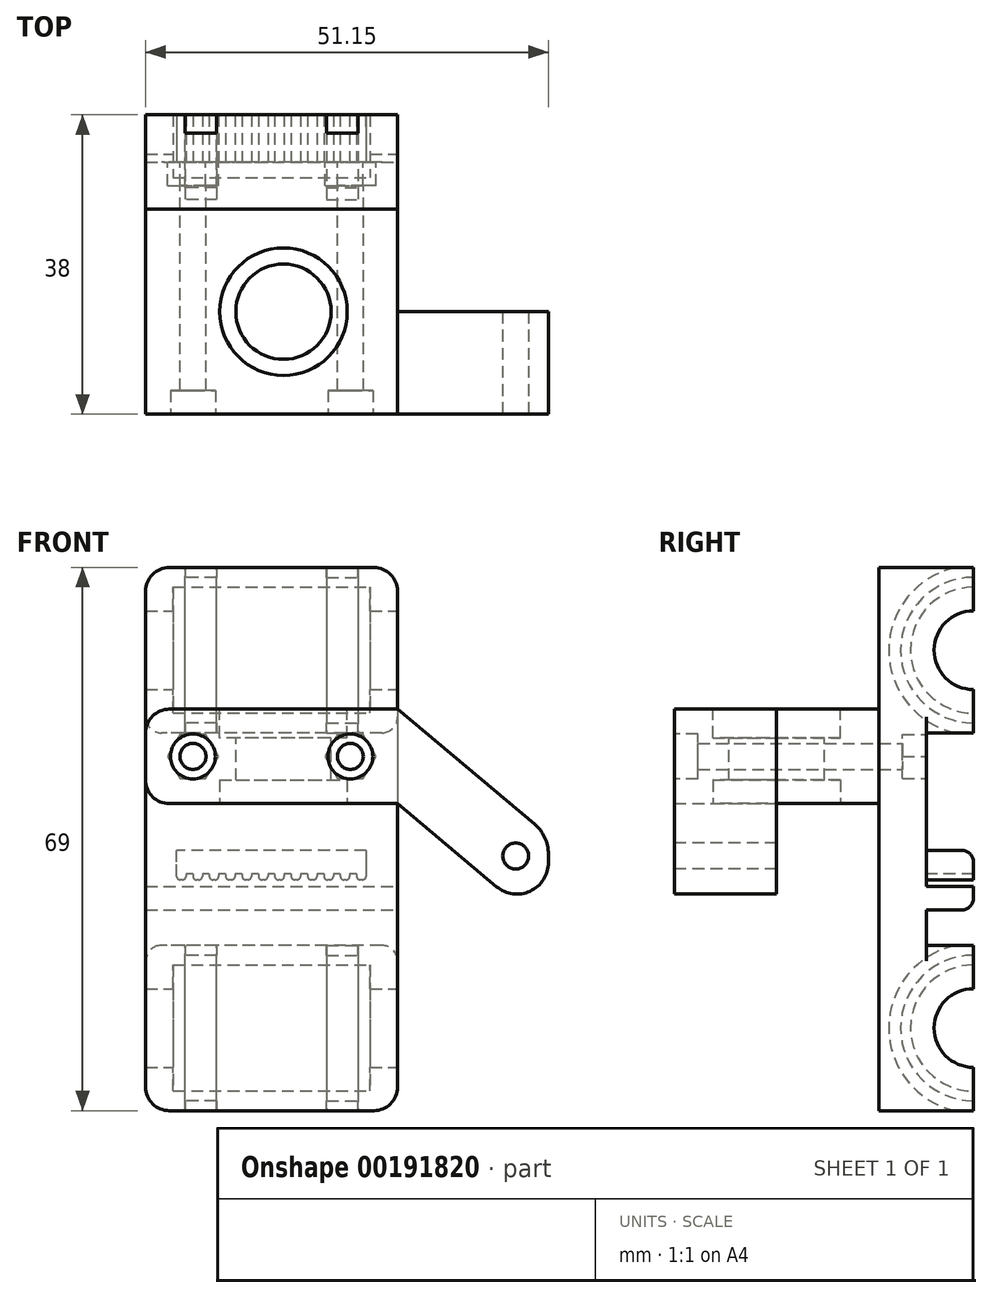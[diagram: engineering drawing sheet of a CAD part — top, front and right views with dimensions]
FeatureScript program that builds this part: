
annotation { "Feature Type Name" : "Feature", "Feature Type Description" : "" }
export const myFeature = defineFeature(function(context is Context, id is Id, definition is map)
    precondition{}
    {
        {
            var Q0;
            Q0=qCreatedBy(makeId("Front.planeOp"),FACE);
            var sketch = newSketch(context, id + "F0", { "sketchPlane" : qUnion([Q0])});
            skLineSegment(sketch, "E0.bottom", {"start": v(-16, 34.5) * mm, "end": v(16, 34.5) * mm});
            skLineSegment(sketch, "E0.top", {"start": v(-16, -34.5) * mm, "end": v(16, -34.5) * mm});
            skLineSegment(sketch, "E0.left", {"start": v(-16, 34.5) * mm, "end": v(-16, -34.5) * mm});
            skLineSegment(sketch, "E0.right", {"start": v(16, 34.5) * mm, "end": v(16, -34.5) * mm});
            skPoint(sketch, "E0.middle", {"position": v(0, 0) * mm});
            skLineSegment(sketch, "E1.bottom", {"start": v(-30, 24) * mm, "end": v(30, 24) * mm, "construction": true});
            skLineSegment(sketch, "E1.top", {"start": v(-30, -24) * mm, "end": v(30, -24) * mm, "construction": true});
            skLineSegment(sketch, "E1.left", {"start": v(-30, 24) * mm, "end": v(-30, -24) * mm, "construction": true});
            skLineSegment(sketch, "E1.right", {"start": v(30, 24) * mm, "end": v(30, -24) * mm, "construction": true});
            skSolve(sketch);
        }
        {
            var Q0;
            Q0=makeQuery(id+"F0.imprint","IMPRINT",FACE,{"disambiguationData":[TD([[makeQuery(id+"F0.imprint","IMPRINT",EDGE,{"derivedFrom":sQuery(id+"F0.wireOp",EDGE,"E0.bottom")}),-1.0]])]});
            extrude(context, id + "F1", {"entities" : qUnion([Q0]), "depth" : 6 * mm});
        }
        {
            var Q0;
            Q0=makeQuery(id+"F0.imprint","IMPRINT",FACE,{"disambiguationData":[TD([[makeQuery(id+"F0.imprint","IMPRINT",EDGE,{"derivedFrom":sQuery(id+"F0.wireOp",EDGE,"E0.bottom")}),-1.0]])]});
            var sketch = newSketch(context, id + "F2", { "sketchPlane" : qUnion([Q0])});
            skLineSegment(sketch, "E2.bottom", {"start": v(16, 34.5) * mm, "end": v(-16, 34.5) * mm});
            skLineSegment(sketch, "E2.top", {"start": v(16, 13.5) * mm, "end": v(-16, 13.5) * mm});
            skLineSegment(sketch, "E2.left", {"start": v(16, 34.5) * mm, "end": v(16, 13.5) * mm});
            skLineSegment(sketch, "E2.right", {"start": v(-16, 34.5) * mm, "end": v(-16, 13.5) * mm});
            skPoint(sketch, "E2.middle", {"position": v(0, 24) * mm});
            skLineSegment(sketch, "E3.bottom", {"start": v(16, -13.5) * mm, "end": v(-16, -13.5) * mm});
            skLineSegment(sketch, "E3.top", {"start": v(16, -34.5) * mm, "end": v(-16, -34.5) * mm});
            skLineSegment(sketch, "E3.left", {"start": v(16, -13.5) * mm, "end": v(16, -34.5) * mm});
            skLineSegment(sketch, "E3.right", {"start": v(-16, -13.5) * mm, "end": v(-16, -34.5) * mm});
            skPoint(sketch, "E3.middle", {"position": v(0, -24) * mm});
            skSolve(sketch);
        }
        {
            var Q0;
            Q0=makeQuery(id+"F2.imprint","IMPRINT",FACE,{"disambiguationData":[TD([[makeQuery(id+"F2.imprint","IMPRINT",EDGE,{"derivedFrom":sQuery(id+"F2.wireOp",EDGE,"E2.bottom")}),-1.0]])]});
            var Q1;
            Q1=makeQuery(id+"F2.imprint","IMPRINT",FACE,{"disambiguationData":[TD([[makeQuery(id+"F2.imprint","IMPRINT",EDGE,{"derivedFrom":sQuery(id+"F2.wireOp",EDGE,"E3.bottom")}),1.0]])]});
            extrude(context, id + "F3", {"entities" : qUnion([Q0, Q1]), "operationType" : NewBodyOperationType.ADD, "oppositeDirection" : true, "depth" : 6 * mm});
        }
        {
            var Q0;
            Q0=makeQuery(id+"F3.boolean.opBoolean","MERGE",FACE,{"derivedFrom":[makeQuery(id+"F1.opExtrude","SWEPT_FACE",FACE,{"disambiguationData":[OSD([sQuery(id+"F0.wireOp",EDGE,"E0.right")])]}),makeQuery(id+"F3.opExtrude","SWEPT_FACE",FACE,{"disambiguationData":[OSD([sQuery(id+"F2.wireOp",EDGE,"E2.left")])]}),makeQuery(id+"F3.opExtrude","SWEPT_FACE",FACE,{"disambiguationData":[OSD([sQuery(id+"F2.wireOp",EDGE,"E3.left")])]})]});
            cPlane(context, id + "F4", {"entities" : qUnion([Q0]), "cplaneType" : CPlaneType.OFFSET, "offset" : 3.5 * mm, "oppositeDirection" : true, "width" : 150 * mm, "height" : 150 * mm});
        }
        {
            var Q0;
            Q0=qCreatedBy(id+"F4.planeOp",FACE);
            var sketch = newSketch(context, id + "F5", { "sketchPlane" : qUnion([Q0])});
            skCircle(sketch, "E4", {"center": v(6, 24) * mm, "radius": 8 * mm});
            skCircle(sketch, "E5", {"center": v(6, -24) * mm, "radius": 8 * mm});
            skSolve(sketch);
        }
        {
            var Q0;
            Q0=makeQuery(id+"F5.imprint","IMPRINT",FACE,{"disambiguationData":[TD([[makeQuery(id+"F5.imprint","IMPRINT",EDGE,{"derivedFrom":sQuery(id+"F5.wireOp",EDGE,"E4")}),1.0]])]});
            var Q1;
            Q1=makeQuery(id+"F5.imprint","IMPRINT",FACE,{"disambiguationData":[TD([[makeQuery(id+"F5.imprint","IMPRINT",EDGE,{"derivedFrom":sQuery(id+"F5.wireOp",EDGE,"E5")}),1.0]])]});
            extrude(context, id + "F6", {"entities" : qUnion([Q0, Q1]), "operationType" : NewBodyOperationType.REMOVE, "oppositeDirection" : true, "depth" : 25 * mm});
        }
        {
            var Q0;
            Q0=makeQuery(id+"F3.boolean.opBoolean","MERGE",FACE,{"derivedFrom":[makeQuery(id+"F1.opExtrude","SWEPT_FACE",FACE,{"disambiguationData":[OSD([sQuery(id+"F0.wireOp",EDGE,"E0.right")])]}),makeQuery(id+"F3.opExtrude","SWEPT_FACE",FACE,{"disambiguationData":[OSD([sQuery(id+"F2.wireOp",EDGE,"E2.left")])]}),makeQuery(id+"F3.opExtrude","SWEPT_FACE",FACE,{"disambiguationData":[OSD([sQuery(id+"F2.wireOp",EDGE,"E3.left")])]})]});
            var sketch = newSketch(context, id + "F7", { "sketchPlane" : qUnion([Q0])});
            skCircle(sketch, "E6", {"center": v(6, 24) * mm, "radius": 5 * mm});
            skCircle(sketch, "E7", {"center": v(6, -24) * mm, "radius": 5 * mm});
            skSolve(sketch);
        }
        {
            var Q0;
            {var subQ0=sQuery(id+"F7.wireOp",EDGE,"E6");var subQ1=makeQuery(id+"F3.opExtrude","CAP_EDGE",EDGE,{"disambiguationData":[OSD([sQuery(id+"F2.wireOp",EDGE,"E2.left")])],"isStart":false});var subQ2=makeQuery(id+"F7.imprint","INTERSECT",VERTEX,{"disambiguationData":[OD(0.0)],"derivedFrom":[subQ1,subQ0]});Q0=makeQuery(id+"F7.imprint","IMPRINT",FACE,{"disambiguationData":[TD([[makeQuery(id+"F7.imprint","IMPRINT",EDGE,{"disambiguationData":[TD([[subQ2,-1.0]])],"derivedFrom":subQ0}),1.0]])]});}
            var Q1;
            {var subQ0=sQuery(id+"F7.wireOp",EDGE,"E7");var subQ1=makeQuery(id+"F3.opExtrude","CAP_EDGE",EDGE,{"disambiguationData":[OSD([sQuery(id+"F2.wireOp",EDGE,"E3.left")])],"isStart":false});var subQ2=makeQuery(id+"F7.imprint","INTERSECT",VERTEX,{"disambiguationData":[OD(0.0)],"derivedFrom":[subQ1,subQ0]});Q1=makeQuery(id+"F7.imprint","IMPRINT",FACE,{"disambiguationData":[TD([[makeQuery(id+"F7.imprint","IMPRINT",EDGE,{"disambiguationData":[TD([[subQ2,1.0]])],"derivedFrom":subQ0}),1.0]])]});}
            var Q2;
            Q2=makeQuery(id+"F3.boolean.opBoolean","MERGE",FACE,{"derivedFrom":[makeQuery(id+"F1.opExtrude","SWEPT_FACE",FACE,{"disambiguationData":[OSD([sQuery(id+"F0.wireOp",EDGE,"E0.left")])]}),makeQuery(id+"F3.opExtrude","SWEPT_FACE",FACE,{"disambiguationData":[OSD([sQuery(id+"F2.wireOp",EDGE,"E2.right")])]}),makeQuery(id+"F3.opExtrude","SWEPT_FACE",FACE,{"disambiguationData":[OSD([sQuery(id+"F2.wireOp",EDGE,"E3.right")])]})]});
            extrude(context, id + "F8", {"entities" : qUnion([Q0, Q1]), "operationType" : NewBodyOperationType.REMOVE, "endBound" : BoundingType.UP_TO_SURFACE, "oppositeDirection" : true, "endBoundEntityFace" : qUnion([Q2]), "depth" : 25 * mm});
        }
        {
            var Q0;
            Q0=makeQuery(id+"F3.boolean.opBoolean","MERGE",FACE,{"derivedFrom":[makeQuery(id+"F1.opExtrude","SWEPT_FACE",FACE,{"disambiguationData":[OSD([sQuery(id+"F0.wireOp",EDGE,"E0.right")])]}),makeQuery(id+"F3.opExtrude","SWEPT_FACE",FACE,{"disambiguationData":[OSD([sQuery(id+"F2.wireOp",EDGE,"E2.left")])]}),makeQuery(id+"F3.opExtrude","SWEPT_FACE",FACE,{"disambiguationData":[OSD([sQuery(id+"F2.wireOp",EDGE,"E3.left")])]})]});
            cPlane(context, id + "F9", {"entities" : qUnion([Q0]), "cplaneType" : CPlaneType.OFFSET, "offset" : 5 * mm, "oppositeDirection" : true, "width" : 150 * mm, "height" : 150 * mm});
        }
        {
            var Q0;
            Q0=makeQuery(id+"F3.boolean.opBoolean","MERGE",FACE,{"derivedFrom":[makeQuery(id+"F1.opExtrude","SWEPT_FACE",FACE,{"disambiguationData":[OSD([sQuery(id+"F0.wireOp",EDGE,"E0.left")])]}),makeQuery(id+"F3.opExtrude","SWEPT_FACE",FACE,{"disambiguationData":[OSD([sQuery(id+"F2.wireOp",EDGE,"E2.right")])]}),makeQuery(id+"F3.opExtrude","SWEPT_FACE",FACE,{"disambiguationData":[OSD([sQuery(id+"F2.wireOp",EDGE,"E3.right")])]})]});
            cPlane(context, id + "F10", {"entities" : qUnion([Q0]), "cplaneType" : CPlaneType.OFFSET, "offset" : 5 * mm, "oppositeDirection" : true, "width" : 150 * mm, "height" : 150 * mm});
        }
        {
            var Q0;
            Q0=qCreatedBy(id+"F9.planeOp",FACE);
            var sketch = newSketch(context, id + "F11", { "sketchPlane" : qUnion([Q0])});
            skCircle(sketch, "E8", {"center": v(6, 24) * mm, "radius": 9.25 * mm});
            skCircle(sketch, "E9", {"center": v(6, 24) * mm, "radius": 10.75 * mm});
            skCircle(sketch, "E10", {"center": v(6, -24) * mm, "radius": 10.75 * mm});
            skCircle(sketch, "E11", {"center": v(6, -24) * mm, "radius": 9.25 * mm});
            skSolve(sketch);
        }
        {
            var Q0;
            Q0=makeQuery(id+"F11.imprint","IMPRINT",FACE,{"disambiguationData":[TD([[makeQuery(id+"F11.imprint","IMPRINT",EDGE,{"derivedFrom":sQuery(id+"F11.wireOp",EDGE,"E8")}),-1.0]])]});
            var Q1;
            Q1=makeQuery(id+"F11.imprint","IMPRINT",FACE,{"disambiguationData":[TD([[makeQuery(id+"F11.imprint","IMPRINT",EDGE,{"derivedFrom":sQuery(id+"F11.wireOp",EDGE,"E10")}),1.0]])]});
            extrude(context, id + "F12", {"entities" : qUnion([Q0, Q1]), "operationType" : NewBodyOperationType.REMOVE, "oppositeDirection" : true, "depth" : 4 * mm});
        }
        {
            var Q0;
            Q0=qCreatedBy(id+"F10.planeOp",FACE);
            var sketch = newSketch(context, id + "F13", { "sketchPlane" : qUnion([Q0])});
            skCircle(sketch, "E12", {"center": v(-6, 24) * mm, "radius": 10.75 * mm});
            skCircle(sketch, "E13", {"center": v(-6, 24) * mm, "radius": 9.25 * mm});
            skCircle(sketch, "E14", {"center": v(-6, -24) * mm, "radius": 10.75 * mm});
            skCircle(sketch, "E15", {"center": v(-6, -24) * mm, "radius": 9.25 * mm});
            skSolve(sketch);
        }
        {
            var Q0;
            Q0=makeQuery(id+"F13.imprint","IMPRINT",FACE,{"disambiguationData":[TD([[makeQuery(id+"F13.imprint","IMPRINT",EDGE,{"derivedFrom":sQuery(id+"F13.wireOp",EDGE,"E12")}),1.0]])]});
            var Q1;
            Q1=makeQuery(id+"F13.imprint","IMPRINT",FACE,{"disambiguationData":[TD([[makeQuery(id+"F13.imprint","IMPRINT",EDGE,{"derivedFrom":sQuery(id+"F13.wireOp",EDGE,"E14")}),1.0]])]});
            extrude(context, id + "F14", {"entities" : qUnion([Q0, Q1]), "operationType" : NewBodyOperationType.REMOVE, "oppositeDirection" : true, "depth" : 4 * mm});
        }
        {
            var Q0;
            Q0=makeQuery(id+"F3.opExtrude","SWEPT_EDGE",EDGE,{"disambiguationData":[OSD([sQuery(id+"F0.wireOp",EDGE,"E0.right"),sQuery(id+"F2.wireOp",EDGE,"E2.top"),sQuery(id+"F2.wireOp",EDGE,"E2.left")])]});
            var Q1;
            Q1=makeQuery(id+"F3.opExtrude","SWEPT_EDGE",EDGE,{"disambiguationData":[OSD([sQuery(id+"F0.wireOp",EDGE,"E0.left"),sQuery(id+"F2.wireOp",EDGE,"E2.top"),sQuery(id+"F2.wireOp",EDGE,"E2.right")])]});
            var Q2;
            Q2=makeQuery(id+"F3.opExtrude","SWEPT_EDGE",EDGE,{"disambiguationData":[OSD([sQuery(id+"F0.wireOp",EDGE,"E0.right"),sQuery(id+"F2.wireOp",EDGE,"E3.bottom"),sQuery(id+"F2.wireOp",EDGE,"E3.left")])]});
            var Q3;
            Q3=makeQuery(id+"F3.opExtrude","SWEPT_EDGE",EDGE,{"disambiguationData":[OSD([sQuery(id+"F0.wireOp",EDGE,"E0.left"),sQuery(id+"F2.wireOp",EDGE,"E3.bottom"),sQuery(id+"F2.wireOp",EDGE,"E3.right")])]});
            fillet(context, id + "F15", {"entities" : qUnion([Q0, Q1, Q2, Q3]), "radius" : 2 * mm, "tangentPropagation" : true, "allowEdgeOverflow" : false});
        }
        {
            var Q0;
            Q0=makeQuery(id+"F3.boolean.opBoolean","MERGE",EDGE,{"derivedFrom":[makeQuery(id+"F1.opExtrude","SWEPT_EDGE",EDGE,{"disambiguationData":[OSD([sQuery(id+"F0.wireOp",EDGE,"E0.top"),sQuery(id+"F0.wireOp",EDGE,"E0.right")])]}),makeQuery(id+"F3.opExtrude","SWEPT_EDGE",EDGE,{"disambiguationData":[OSD([sQuery(id+"F2.wireOp",EDGE,"E3.top"),sQuery(id+"F2.wireOp",EDGE,"E3.left")])]})]});
            var Q1;
            Q1=makeQuery(id+"F3.boolean.opBoolean","MERGE",EDGE,{"derivedFrom":[makeQuery(id+"F1.opExtrude","SWEPT_EDGE",EDGE,{"disambiguationData":[OSD([sQuery(id+"F0.wireOp",EDGE,"E0.top"),sQuery(id+"F0.wireOp",EDGE,"E0.left")])]}),makeQuery(id+"F3.opExtrude","SWEPT_EDGE",EDGE,{"disambiguationData":[OSD([sQuery(id+"F2.wireOp",EDGE,"E3.top"),sQuery(id+"F2.wireOp",EDGE,"E3.right")])]})]});
            var Q2;
            Q2=makeQuery(id+"F3.boolean.opBoolean","MERGE",EDGE,{"derivedFrom":[makeQuery(id+"F1.opExtrude","SWEPT_EDGE",EDGE,{"disambiguationData":[OSD([sQuery(id+"F0.wireOp",EDGE,"E0.bottom"),sQuery(id+"F0.wireOp",EDGE,"E0.right")])]}),makeQuery(id+"F3.opExtrude","SWEPT_EDGE",EDGE,{"disambiguationData":[OSD([sQuery(id+"F2.wireOp",EDGE,"E2.bottom"),sQuery(id+"F2.wireOp",EDGE,"E2.left")])]})]});
            var Q3;
            Q3=makeQuery(id+"F3.boolean.opBoolean","MERGE",EDGE,{"derivedFrom":[makeQuery(id+"F1.opExtrude","SWEPT_EDGE",EDGE,{"disambiguationData":[OSD([sQuery(id+"F0.wireOp",EDGE,"E0.bottom"),sQuery(id+"F0.wireOp",EDGE,"E0.left")])]}),makeQuery(id+"F3.opExtrude","SWEPT_EDGE",EDGE,{"disambiguationData":[OSD([sQuery(id+"F2.wireOp",EDGE,"E2.bottom"),sQuery(id+"F2.wireOp",EDGE,"E2.right")])]})]});
            fillet(context, id + "F16", {"entities" : qUnion([Q0, Q1, Q2, Q3]), "radius" : 3 * mm, "tangentPropagation" : true, "allowEdgeOverflow" : false});
        }
        {
            var Q0;
            Q0=makeQuery(id+"F1.opExtrude","CAP_FACE",FACE,{"disambiguationData":[OSD([sQuery(id+"F0.wireOp",EDGE,"E0.bottom"),sQuery(id+"F0.wireOp",EDGE,"E0.top"),sQuery(id+"F0.wireOp",EDGE,"E0.left"),sQuery(id+"F0.wireOp",EDGE,"E0.right")])],"isStart":true});
            var sketch = newSketch(context, id + "F17", { "sketchPlane" : qUnion([Q0])});
            skCircle(sketch, "E16", {"center": v(-10, 10.5) * mm, "radius": 1.65 * mm});
            skCircle(sketch, "E17", {"center": v(10, 10.5) * mm, "radius": 1.65 * mm});
            skCircle(sketch, "E18.cCircle", {"center": v(-10, 10.5) * mm, "radius": 2.8 * mm, "construction": true});
            skLineSegment(sketch, "E18.0", {"start": v(-13.23, 10.5) * mm, "end": v(-11.62, 13.3) * mm});
            skLineSegment(sketch, "E18.1", {"start": v(-11.62, 13.3) * mm, "end": v(-8.38, 13.3) * mm});
            skLineSegment(sketch, "E18.2", {"start": v(-8.38, 13.3) * mm, "end": v(-6.77, 10.5) * mm});
            skLineSegment(sketch, "E18.3", {"start": v(-6.77, 10.5) * mm, "end": v(-8.38, 7.7) * mm});
            skLineSegment(sketch, "E18.4", {"start": v(-8.38, 7.7) * mm, "end": v(-11.62, 7.7) * mm});
            skLineSegment(sketch, "E18.5", {"start": v(-11.62, 7.7) * mm, "end": v(-13.23, 10.5) * mm});
            skPoint(sketch, "E18.0.midPoint", {"position": v(-12.42, 11.9) * mm});
            skCircle(sketch, "E19.cCircle", {"center": v(10, 10.5) * mm, "radius": 2.8 * mm, "construction": true});
            skLineSegment(sketch, "E19.0", {"start": v(6.77, 10.5) * mm, "end": v(8.38, 13.3) * mm});
            skLineSegment(sketch, "E19.1", {"start": v(8.38, 13.3) * mm, "end": v(11.62, 13.3) * mm});
            skLineSegment(sketch, "E19.2", {"start": v(11.62, 13.3) * mm, "end": v(13.23, 10.5) * mm});
            skLineSegment(sketch, "E19.3", {"start": v(13.23, 10.5) * mm, "end": v(11.62, 7.7) * mm});
            skLineSegment(sketch, "E19.4", {"start": v(11.62, 7.7) * mm, "end": v(8.38, 7.7) * mm});
            skLineSegment(sketch, "E19.5", {"start": v(8.38, 7.7) * mm, "end": v(6.77, 10.5) * mm});
            skPoint(sketch, "E19.0.midPoint", {"position": v(7.58, 11.9) * mm});
            skSolve(sketch);
        }
        {
            var Q0;
            Q0=makeQuery(id+"F17.imprint","IMPRINT",FACE,{"disambiguationData":[TD([[makeQuery(id+"F17.imprint","IMPRINT",EDGE,{"derivedFrom":sQuery(id+"F17.wireOp",EDGE,"E16")}),1.0]])]});
            var Q1;
            Q1=makeQuery(id+"F17.imprint","IMPRINT",FACE,{"disambiguationData":[TD([[makeQuery(id+"F17.imprint","IMPRINT",EDGE,{"derivedFrom":sQuery(id+"F17.wireOp",EDGE,"E17")}),1.0]])]});
            extrude(context, id + "F18", {"entities" : qUnion([Q0, Q1]), "operationType" : NewBodyOperationType.REMOVE, "endBound" : BoundingType.THROUGH_ALL, "oppositeDirection" : true, "depth" : 25 * mm});
        }
        {
            var Q0;
            Q0=makeQuery(id+"F17.imprint","IMPRINT",FACE,{"disambiguationData":[TD([[makeQuery(id+"F17.imprint","IMPRINT",EDGE,{"derivedFrom":sQuery(id+"F17.wireOp",EDGE,"E16")}),-1.0]])]});
            var Q1;
            Q1=makeQuery(id+"F17.imprint","IMPRINT",FACE,{"disambiguationData":[TD([[makeQuery(id+"F17.imprint","IMPRINT",EDGE,{"derivedFrom":sQuery(id+"F17.wireOp",EDGE,"E17")}),-1.0]])]});
            extrude(context, id + "F19", {"entities" : qUnion([Q0, Q1]), "operationType" : NewBodyOperationType.REMOVE, "oppositeDirection" : true, "depth" : 3 * mm});
        }
        {
            var Q0;
            Q0=makeQuery(id+"F1.opExtrude","CAP_FACE",FACE,{"disambiguationData":[OSD([sQuery(id+"F0.wireOp",EDGE,"E0.bottom"),sQuery(id+"F0.wireOp",EDGE,"E0.top"),sQuery(id+"F0.wireOp",EDGE,"E0.left"),sQuery(id+"F0.wireOp",EDGE,"E0.right")])],"isStart":false});
            var sketch = newSketch(context, id + "F20", { "sketchPlane" : qUnion([Q0])});
            skLineSegment(sketch, "E20.bottom", {"start": v(-16, 16.5) * mm, "end": v(16, 16.5) * mm});
            skLineSegment(sketch, "E20.top", {"start": v(-16, 4.5) * mm, "end": v(16, 4.5) * mm});
            skLineSegment(sketch, "E20.left", {"start": v(-16, 16.5) * mm, "end": v(-16, 4.5) * mm});
            skLineSegment(sketch, "E20.right", {"start": v(16, 16.5) * mm, "end": v(16, 4.5) * mm});
            skSolve(sketch);
        }
        {
            var Q0;
            Q0=makeQuery(id+"F20.imprint","IMPRINT",FACE,{"disambiguationData":[TD([[makeQuery(id+"F20.imprint","IMPRINT",EDGE,{"derivedFrom":sQuery(id+"F20.wireOp",EDGE,"E20.bottom")}),-1.0]])]});
            extrude(context, id + "F21", {"entities" : qUnion([Q0]), "depth" : (26 / 2) * mm});
        }
        {
            var Q0;
            Q0=makeQuery(id+"F21.opExtrude","CAP_FACE",FACE,{"disambiguationData":[OSD([sQuery(id+"F0.wireOp",EDGE,"E0.bottom"),sQuery(id+"F0.wireOp",EDGE,"E0.top"),sQuery(id+"F0.wireOp",EDGE,"E0.left"),sQuery(id+"F0.wireOp",EDGE,"E0.right"),sQuery(id+"F17.wireOp",EDGE,"E16"),sQuery(id+"F17.wireOp",EDGE,"E17"),sQuery(id+"F20.wireOp",EDGE,"E20.bottom"),sQuery(id+"F20.wireOp",EDGE,"E20.top"),sQuery(id+"F20.wireOp",EDGE,"E20.left"),sQuery(id+"F20.wireOp",EDGE,"E20.right")])],"isStart":false});
            extrude(context, id + "F22", {"entities" : qUnion([Q0]), "depth" : (26 / 2) * mm});
        }
        {
            var Q0;
            Q0=makeQuery(id+"F21.opExtrude","SWEPT_EDGE",EDGE,{"disambiguationData":[OSD([sQuery(id+"F0.wireOp",EDGE,"E0.left"),sQuery(id+"F20.wireOp",EDGE,"E20.top"),sQuery(id+"F20.wireOp",EDGE,"E20.left")])]});
            var Q1;
            Q1=makeQuery(id+"F22.opExtrude","SWEPT_EDGE",EDGE,{"disambiguationData":[OSD([sQuery(id+"F0.wireOp",EDGE,"E0.left"),sQuery(id+"F20.wireOp",EDGE,"E20.top"),sQuery(id+"F20.wireOp",EDGE,"E20.left")])]});
            var Q2;
            Q2=makeQuery(id+"F22.opExtrude","SWEPT_EDGE",EDGE,{"disambiguationData":[OSD([sQuery(id+"F0.wireOp",EDGE,"E0.left"),sQuery(id+"F20.wireOp",EDGE,"E20.bottom"),sQuery(id+"F20.wireOp",EDGE,"E20.left")])]});
            var Q3;
            Q3=makeQuery(id+"F21.opExtrude","SWEPT_EDGE",EDGE,{"disambiguationData":[OSD([sQuery(id+"F0.wireOp",EDGE,"E0.left"),sQuery(id+"F20.wireOp",EDGE,"E20.bottom"),sQuery(id+"F20.wireOp",EDGE,"E20.left")])]});
            fillet(context, id + "F23", {"entities" : qUnion([Q0, Q1, Q2, Q3]), "radius" : 3 * mm, "tangentPropagation" : true, "allowEdgeOverflow" : false});
        }
        {
            var Q0;
            Q0=makeQuery(id+"F21.opExtrude","SWEPT_FACE",FACE,{"disambiguationData":[OSD([sQuery(id+"F20.wireOp",EDGE,"E20.bottom")])]});
            var sketch = newSketch(context, id + "F24", { "sketchPlane" : qUnion([Q0])});
            skCircle(sketch, "E21", {"center": v(1.5, -19) * mm, "radius": 8.1 * mm});
            skSolve(sketch);
        }
        {
            var Q0;
            {var subQ0=sQuery(id+"F24.wireOp",EDGE,"E21");var subQ1=makeQuery(id+"F21.opExtrude","CAP_EDGE",EDGE,{"disambiguationData":[OSD([sQuery(id+"F20.wireOp",EDGE,"E20.bottom")])],"isStart":false});var subQ2=makeQuery(id+"F24.imprint","INTERSECT",VERTEX,{"disambiguationData":[OD(0.0)],"derivedFrom":[subQ1,subQ0]});Q0=makeQuery(id+"F24.imprint","IMPRINT",FACE,{"disambiguationData":[TD([[makeQuery(id+"F24.imprint","IMPRINT",EDGE,{"disambiguationData":[TD([[subQ2,1.0]])],"derivedFrom":subQ0}),1.0]])]});}
            var Q1;
            {var subQ0=sQuery(id+"F24.wireOp",EDGE,"E21");var subQ1=makeQuery(id+"F21.opExtrude","CAP_EDGE",EDGE,{"disambiguationData":[OSD([sQuery(id+"F20.wireOp",EDGE,"E20.bottom")])],"isStart":false});var subQ2=makeQuery(id+"F24.imprint","INTERSECT",VERTEX,{"disambiguationData":[OD(0.0)],"derivedFrom":[subQ1,subQ0]});Q1=makeQuery(id+"F24.imprint","IMPRINT",FACE,{"disambiguationData":[TD([[makeQuery(id+"F24.imprint","IMPRINT",EDGE,{"disambiguationData":[TD([[subQ2,-1.0]])],"derivedFrom":subQ0}),1.0]])]});}
            extrude(context, id + "F25", {"entities" : qUnion([Q0, Q1]), "operationType" : NewBodyOperationType.REMOVE, "oppositeDirection" : true, "depth" : 3.65 * mm});
        }
        {
            var Q0;
            Q0=makeQuery(id+"F21.opExtrude","SWEPT_FACE",FACE,{"disambiguationData":[OSD([sQuery(id+"F20.wireOp",EDGE,"E20.top")])]});
            var sketch = newSketch(context, id + "F26", { "sketchPlane" : qUnion([Q0])});
            skCircle(sketch, "E22", {"center": v(1.5, 19) * mm, "radius": 8.1 * mm});
            skSolve(sketch);
        }
        {
            var Q0;
            {var subQ0=sQuery(id+"F26.wireOp",EDGE,"E22");var subQ1=makeQuery(id+"F21.opExtrude","CAP_EDGE",EDGE,{"disambiguationData":[OSD([sQuery(id+"F20.wireOp",EDGE,"E20.top")])],"isStart":false});var subQ2=makeQuery(id+"F26.imprint","INTERSECT",VERTEX,{"disambiguationData":[OD(0.0)],"derivedFrom":[subQ1,subQ0]});Q0=makeQuery(id+"F26.imprint","IMPRINT",FACE,{"disambiguationData":[TD([[makeQuery(id+"F26.imprint","IMPRINT",EDGE,{"disambiguationData":[TD([[subQ2,1.0]])],"derivedFrom":subQ0}),1.0]])]});}
            var Q1;
            {var subQ0=sQuery(id+"F26.wireOp",EDGE,"E22");var subQ1=makeQuery(id+"F21.opExtrude","CAP_EDGE",EDGE,{"disambiguationData":[OSD([sQuery(id+"F20.wireOp",EDGE,"E20.top")])],"isStart":false});var subQ2=makeQuery(id+"F26.imprint","INTERSECT",VERTEX,{"disambiguationData":[OD(0.0)],"derivedFrom":[subQ1,subQ0]});Q1=makeQuery(id+"F26.imprint","IMPRINT",FACE,{"disambiguationData":[TD([[makeQuery(id+"F26.imprint","IMPRINT",EDGE,{"disambiguationData":[TD([[subQ2,-1.0]])],"derivedFrom":subQ0}),1.0]])]});}
            extrude(context, id + "F27", {"entities" : qUnion([Q0, Q1]), "operationType" : NewBodyOperationType.REMOVE, "oppositeDirection" : true, "depth" : 3 * mm});
        }
        {
            var Q0;
            {var subQ0=sQuery(id+"F24.wireOp",EDGE,"E21");Q0=makeQuery(id+"F25.boolean.opBoolean","COPY",FACE,{"disambiguationData":[TD([makeQuery(id+"F21.opExtrude","CAP_FACE",FACE,{"disambiguationData":[OSD([sQuery(id+"F0.wireOp",EDGE,"E0.bottom"),sQuery(id+"F0.wireOp",EDGE,"E0.top"),sQuery(id+"F0.wireOp",EDGE,"E0.left"),sQuery(id+"F0.wireOp",EDGE,"E0.right"),sQuery(id+"F17.wireOp",EDGE,"E16"),sQuery(id+"F17.wireOp",EDGE,"E17"),sQuery(id+"F20.wireOp",EDGE,"E20.bottom"),sQuery(id+"F20.wireOp",EDGE,"E20.top"),sQuery(id+"F20.wireOp",EDGE,"E20.left"),sQuery(id+"F20.wireOp",EDGE,"E20.right")])],"isStart":false})])],"derivedFrom":makeQuery(id+"F25.opExtrude","CAP_FACE",FACE,{"disambiguationData":[OSD([subQ0])],"isStart":false})});}
            var sketch = newSketch(context, id + "F28", { "sketchPlane" : qUnion([Q0])});
            skCircle(sketch, "E23", {"center": v(1.5, -19) * mm, "radius": 6.05 * mm});
            skSolve(sketch);
        }
        {
            var Q0;
            {var subQ0=sQuery(id+"F28.wireOp",EDGE,"E23");var subQ1=makeQuery(id+"F25.boolean.opBoolean","INTERSECT",EDGE,{"derivedFrom":[makeQuery(id+"F21.opExtrude","CAP_FACE",FACE,{"disambiguationData":[OSD([sQuery(id+"F0.wireOp",EDGE,"E0.bottom"),sQuery(id+"F0.wireOp",EDGE,"E0.top"),sQuery(id+"F0.wireOp",EDGE,"E0.left"),sQuery(id+"F0.wireOp",EDGE,"E0.right"),sQuery(id+"F17.wireOp",EDGE,"E16"),sQuery(id+"F17.wireOp",EDGE,"E17"),sQuery(id+"F20.wireOp",EDGE,"E20.bottom"),sQuery(id+"F20.wireOp",EDGE,"E20.top"),sQuery(id+"F20.wireOp",EDGE,"E20.left"),sQuery(id+"F20.wireOp",EDGE,"E20.right")])],"isStart":false}),makeQuery(id+"F25.opExtrude","CAP_FACE",FACE,{"disambiguationData":[OSD([sQuery(id+"F24.wireOp",EDGE,"E21")])],"isStart":false})]});var subQ2=makeQuery(id+"F28.imprint","INTERSECT",VERTEX,{"disambiguationData":[OD(0.0)],"derivedFrom":[subQ1,subQ0]});Q0=makeQuery(id+"F28.imprint","IMPRINT",FACE,{"disambiguationData":[TD([[makeQuery(id+"F28.imprint","IMPRINT",EDGE,{"disambiguationData":[TD([[subQ2,1.0]])],"derivedFrom":subQ0}),1.0]])]});}
            var Q1;
            {var subQ0=sQuery(id+"F28.wireOp",EDGE,"E23");var subQ1=makeQuery(id+"F25.boolean.opBoolean","INTERSECT",EDGE,{"derivedFrom":[makeQuery(id+"F21.opExtrude","CAP_FACE",FACE,{"disambiguationData":[OSD([sQuery(id+"F0.wireOp",EDGE,"E0.bottom"),sQuery(id+"F0.wireOp",EDGE,"E0.top"),sQuery(id+"F0.wireOp",EDGE,"E0.left"),sQuery(id+"F0.wireOp",EDGE,"E0.right"),sQuery(id+"F17.wireOp",EDGE,"E16"),sQuery(id+"F17.wireOp",EDGE,"E17"),sQuery(id+"F20.wireOp",EDGE,"E20.bottom"),sQuery(id+"F20.wireOp",EDGE,"E20.top"),sQuery(id+"F20.wireOp",EDGE,"E20.left"),sQuery(id+"F20.wireOp",EDGE,"E20.right")])],"isStart":false}),makeQuery(id+"F25.opExtrude","CAP_FACE",FACE,{"disambiguationData":[OSD([sQuery(id+"F24.wireOp",EDGE,"E21")])],"isStart":false})]});var subQ2=makeQuery(id+"F28.imprint","INTERSECT",VERTEX,{"disambiguationData":[OD(0.0)],"derivedFrom":[subQ1,subQ0]});Q1=makeQuery(id+"F28.imprint","IMPRINT",FACE,{"disambiguationData":[TD([[makeQuery(id+"F28.imprint","IMPRINT",EDGE,{"disambiguationData":[TD([[subQ2,-1.0]])],"derivedFrom":subQ0}),1.0]])]});}
            extrude(context, id + "F29", {"entities" : qUnion([Q0, Q1]), "operationType" : NewBodyOperationType.REMOVE, "oppositeDirection" : true, "depth" : 25 * mm});
        }
        {
            var Q0;
            Q0=makeQuery(id+"F22.opExtrude","CAP_FACE",FACE,{"disambiguationData":[OSD([sQuery(id+"F0.wireOp",EDGE,"E0.bottom"),sQuery(id+"F0.wireOp",EDGE,"E0.top"),sQuery(id+"F0.wireOp",EDGE,"E0.left"),sQuery(id+"F0.wireOp",EDGE,"E0.right"),sQuery(id+"F17.wireOp",EDGE,"E16"),sQuery(id+"F17.wireOp",EDGE,"E17"),sQuery(id+"F20.wireOp",EDGE,"E20.bottom"),sQuery(id+"F20.wireOp",EDGE,"E20.top"),sQuery(id+"F20.wireOp",EDGE,"E20.left"),sQuery(id+"F20.wireOp",EDGE,"E20.right")])],"isStart":false});
            var sketch = newSketch(context, id + "F30", { "sketchPlane" : qUnion([Q0])});
            skCircle(sketch, "E24", {"center": v(-10, 10.5) * mm, "radius": 2.85 * mm});
            skCircle(sketch, "E25", {"center": v(10, 10.5) * mm, "radius": 2.85 * mm});
            skSolve(sketch);
        }
        {
            var Q0;
            Q0=qSketchRegion(id+"F30",true);
            extrude(context, id + "F31", {"entities" : qUnion([Q0]), "operationType" : NewBodyOperationType.REMOVE, "oppositeDirection" : true, "depth" : 3 * mm});
        }
        {
            var Q0;
            Q0=makeQuery(id+"F0.imprint","IMPRINT",FACE,{"disambiguationData":[TD([[makeQuery(id+"F0.imprint","IMPRINT",EDGE,{"derivedFrom":sQuery(id+"F0.wireOp",EDGE,"E0.bottom")}),-1.0]])]});
            var sketch = newSketch(context, id + "F32", { "sketchPlane" : qUnion([Q0])});
            skLineSegment(sketch, "E26.bottom", {"start": v(-16, -9) * mm, "end": v(16, -9) * mm});
            skLineSegment(sketch, "E26.top", {"start": v(-16, -6) * mm, "end": v(16, -6) * mm});
            skLineSegment(sketch, "E26.left", {"start": v(-16, -9) * mm, "end": v(-16, -6) * mm});
            skLineSegment(sketch, "E26.right", {"start": v(16, -9) * mm, "end": v(16, -6) * mm});
            skLineSegment(sketch, "E27.bottom", {"start": v(12, -1.42) * mm, "end": v(-12, -1.42) * mm});
            skLineSegment(sketch, "E27.top", {"start": v(12, -4.42) * mm, "end": v(-12, -4.42) * mm});
            skLineSegment(sketch, "E27.left", {"start": v(12, -1.42) * mm, "end": v(12, -4.42) * mm});
            skLineSegment(sketch, "E27.right", {"start": v(-12, -1.42) * mm, "end": v(-12, -4.42) * mm});
            skLineSegment(sketch, "E28", {"start": v(7.4, -5.17) * mm, "end": v(7.1, -5.17) * mm});
            skLineSegment(sketch, "E29.bottom", {"start": v(12, -4.42) * mm, "end": v(10.8, -4.42) * mm, "construction": true});
            skLineSegment(sketch, "E29.top", {"start": v(11.55, -5.17) * mm, "end": v(11.25, -5.17) * mm});
            skLineSegment(sketch, "E29.left", {"start": v(12, -4.42) * mm, "end": v(12, -4.72) * mm});
            skLineSegment(sketch, "E29.right", {"start": v(10.8, -4.42) * mm, "end": v(10.8, -4.72) * mm});
            skLineSegment(sketch, "E30.bottom", {"start": v(9.92, -4.42) * mm, "end": v(8.72, -4.42) * mm, "construction": true});
            skLineSegment(sketch, "E30.top", {"start": v(9.92, -5.17) * mm, "end": v(8.72, -5.17) * mm});
            skLineSegment(sketch, "E30.left", {"start": v(9.92, -4.42) * mm, "end": v(9.92, -4.72) * mm});
            skLineSegment(sketch, "E30.right", {"start": v(8.72, -4.42) * mm, "end": v(8.72, -4.72) * mm});
            skLineSegment(sketch, "E31.1.0.0", {"start": v(7.84, -4.42) * mm, "end": v(7.84, -4.72) * mm});
            skLineSegment(sketch, "E31.1.0.1", {"start": v(6.64, -4.42) * mm, "end": v(6.64, -4.72) * mm});
            skLineSegment(sketch, "E31.2.0.0", {"start": v(5.76, -4.42) * mm, "end": v(5.76, -4.72) * mm});
            skLineSegment(sketch, "E31.2.0.1", {"start": v(4.56, -4.42) * mm, "end": v(4.56, -4.72) * mm});
            skLineSegment(sketch, "E31.3.0.0", {"start": v(3.68, -4.42) * mm, "end": v(3.68, -4.72) * mm});
            skLineSegment(sketch, "E31.3.0.1", {"start": v(2.48, -4.42) * mm, "end": v(2.48, -4.72) * mm});
            skLineSegment(sketch, "E31.4.0.0", {"start": v(1.6, -4.42) * mm, "end": v(1.6, -4.72) * mm});
            skLineSegment(sketch, "E31.4.0.1", {"start": v(0.4, -4.42) * mm, "end": v(0.4, -4.72) * mm});
            skLineSegment(sketch, "E31.5.0.0", {"start": v(-0.48, -4.42) * mm, "end": v(-0.48, -4.72) * mm});
            skLineSegment(sketch, "E31.5.0.1", {"start": v(-1.68, -4.42) * mm, "end": v(-1.68, -4.72) * mm});
            skLineSegment(sketch, "E31.6.0.0", {"start": v(-2.56, -4.42) * mm, "end": v(-2.56, -4.72) * mm});
            skLineSegment(sketch, "E31.6.0.1", {"start": v(-3.76, -4.42) * mm, "end": v(-3.76, -4.72) * mm});
            skLineSegment(sketch, "E31.7.0.0", {"start": v(-4.64, -4.42) * mm, "end": v(-4.64, -4.72) * mm});
            skLineSegment(sketch, "E31.7.0.1", {"start": v(-5.84, -4.42) * mm, "end": v(-5.84, -4.72) * mm});
            skLineSegment(sketch, "E31.8.0.0", {"start": v(-6.72, -4.42) * mm, "end": v(-6.72, -4.72) * mm});
            skLineSegment(sketch, "E31.8.0.1", {"start": v(-7.92, -4.42) * mm, "end": v(-7.92, -4.72) * mm});
            skLineSegment(sketch, "E31.9.0.0", {"start": v(-8.8, -4.42) * mm, "end": v(-8.8, -4.72) * mm});
            skLineSegment(sketch, "E31.9.0.1", {"start": v(-10, -4.42) * mm, "end": v(-10, -4.72) * mm});
            skLineSegment(sketch, "E31.direction1", {"start": v(9.47, -5.17) * mm, "end": v(9.17, -5.17) * mm, "construction": true});
            skPoint(sketch, "E32.visualSharp", {"position": v(12, -5.17) * mm});
            skArc(sketch, "E32.filletArc", {"start": v(11.55, -5.17) * mm, "mid": v(11.87, -5.04) * mm, "end": v(12, -4.72) * mm});
            skPoint(sketch, "E33.visualSharp", {"position": v(10.8, -5.17) * mm});
            skArc(sketch, "E33.filletArc", {"start": v(10.8, -4.72) * mm, "mid": v(10.93, -5.04) * mm, "end": v(11.25, -5.17) * mm});
            skPoint(sketch, "E34.visualSharp", {"position": v(9.92, -5.17) * mm});
            skArc(sketch, "E34.filletArc", {"start": v(9.47, -5.17) * mm, "mid": v(9.79, -5.04) * mm, "end": v(9.92, -4.72) * mm});
            skPoint(sketch, "E35.newPointA", {"position": v(7.84, -5.17) * mm});
            skPoint(sketch, "E35.newPointB", {"position": v(8.72, -5.17) * mm});
            skArc(sketch, "E35.filletArc", {"start": v(8.72, -4.72) * mm, "mid": v(8.85, -5.04) * mm, "end": v(9.17, -5.17) * mm});
            skPoint(sketch, "E36.newPointB", {"position": v(16, -5.17) * mm});
            skArc(sketch, "E36.filletArc", {"start": v(7.4, -5.17) * mm, "mid": v(7.7, -5.04) * mm, "end": v(7.84, -4.72) * mm});
            skPoint(sketch, "E37.newPointA", {"position": v(-16, -5.17) * mm});
            skPoint(sketch, "E37.newPointB", {"position": v(6.64, -5.17) * mm});
            skArc(sketch, "E37.filletArc", {"start": v(6.64, -4.72) * mm, "mid": v(6.77, -5.04) * mm, "end": v(7.1, -5.17) * mm});
            skLineSegment(sketch, "E38", {"start": v(5.31, -5.17) * mm, "end": v(5.01, -5.17) * mm});
            skLineSegment(sketch, "E39", {"start": v(3.23, -5.17) * mm, "end": v(2.93, -5.17) * mm});
            skLineSegment(sketch, "E40", {"start": v(1.15, -5.17) * mm, "end": v(0.85, -5.17) * mm});
            skLineSegment(sketch, "E41", {"start": v(-0.93, -5.17) * mm, "end": v(-1.23, -5.17) * mm});
            skLineSegment(sketch, "E42", {"start": v(-3, -5.17) * mm, "end": v(-3.3, -5.17) * mm});
            skLineSegment(sketch, "E43", {"start": v(-5.09, -5.17) * mm, "end": v(-5.39, -5.17) * mm});
            skLineSegment(sketch, "E44", {"start": v(-7.17, -5.17) * mm, "end": v(-7.47, -5.17) * mm});
            skLineSegment(sketch, "E45", {"start": v(-9.25, -5.17) * mm, "end": v(-9.55, -5.17) * mm});
            skPoint(sketch, "E46.visualSharp", {"position": v(5.76, -5.17) * mm});
            skArc(sketch, "E46.filletArc", {"start": v(5.31, -5.17) * mm, "mid": v(5.63, -5.04) * mm, "end": v(5.76, -4.72) * mm});
            skPoint(sketch, "E47.visualSharp", {"position": v(4.56, -5.17) * mm});
            skArc(sketch, "E47.filletArc", {"start": v(4.56, -4.72) * mm, "mid": v(4.7, -5.04) * mm, "end": v(5.01, -5.17) * mm});
            skPoint(sketch, "E48.visualSharp", {"position": v(3.68, -5.17) * mm});
            skArc(sketch, "E48.filletArc", {"start": v(3.23, -5.17) * mm, "mid": v(3.55, -5.04) * mm, "end": v(3.68, -4.72) * mm});
            skPoint(sketch, "E49.visualSharp", {"position": v(2.48, -5.17) * mm});
            skArc(sketch, "E49.filletArc", {"start": v(2.48, -4.72) * mm, "mid": v(2.61, -5.04) * mm, "end": v(2.93, -5.17) * mm});
            skPoint(sketch, "E50.visualSharp", {"position": v(1.6, -5.17) * mm});
            skArc(sketch, "E50.filletArc", {"start": v(1.15, -5.17) * mm, "mid": v(1.47, -5.04) * mm, "end": v(1.6, -4.72) * mm});
            skPoint(sketch, "E51.visualSharp", {"position": v(0.4, -5.17) * mm});
            skArc(sketch, "E51.filletArc", {"start": v(0.4, -4.72) * mm, "mid": v(0.53, -5.04) * mm, "end": v(0.85, -5.17) * mm});
            skPoint(sketch, "E52.visualSharp", {"position": v(-0.48, -5.17) * mm});
            skArc(sketch, "E52.filletArc", {"start": v(-0.93, -5.17) * mm, "mid": v(-0.61, -5.04) * mm, "end": v(-0.48, -4.72) * mm});
            skPoint(sketch, "E53.visualSharp", {"position": v(-1.68, -5.17) * mm});
            skArc(sketch, "E53.filletArc", {"start": v(-1.68, -4.72) * mm, "mid": v(-1.55, -5.04) * mm, "end": v(-1.23, -5.17) * mm});
            skPoint(sketch, "E54.visualSharp", {"position": v(-2.56, -5.17) * mm});
            skArc(sketch, "E54.filletArc", {"start": v(-3, -5.17) * mm, "mid": v(-2.7, -5.04) * mm, "end": v(-2.56, -4.72) * mm});
            skPoint(sketch, "E55.visualSharp", {"position": v(-3.76, -5.17) * mm});
            skArc(sketch, "E55.filletArc", {"start": v(-3.76, -4.72) * mm, "mid": v(-3.63, -5.04) * mm, "end": v(-3.3, -5.17) * mm});
            skPoint(sketch, "E56.visualSharp", {"position": v(-4.64, -5.17) * mm});
            skArc(sketch, "E56.filletArc", {"start": v(-5.09, -5.17) * mm, "mid": v(-4.77, -5.04) * mm, "end": v(-4.64, -4.72) * mm});
            skPoint(sketch, "E57.visualSharp", {"position": v(-5.84, -5.17) * mm});
            skArc(sketch, "E57.filletArc", {"start": v(-5.84, -4.72) * mm, "mid": v(-5.7, -5.04) * mm, "end": v(-5.39, -5.17) * mm});
            skPoint(sketch, "E58.visualSharp", {"position": v(-6.72, -5.17) * mm});
            skArc(sketch, "E58.filletArc", {"start": v(-7.17, -5.17) * mm, "mid": v(-6.85, -5.04) * mm, "end": v(-6.72, -4.72) * mm});
            skPoint(sketch, "E59.visualSharp", {"position": v(-8.8, -5.17) * mm});
            skArc(sketch, "E59.filletArc", {"start": v(-9.25, -5.17) * mm, "mid": v(-8.93, -5.04) * mm, "end": v(-8.8, -4.72) * mm});
            skPoint(sketch, "E60.visualSharp", {"position": v(-7.92, -5.17) * mm});
            skArc(sketch, "E60.filletArc", {"start": v(-7.92, -4.72) * mm, "mid": v(-7.79, -5.04) * mm, "end": v(-7.47, -5.17) * mm});
            skPoint(sketch, "E61.visualSharp", {"position": v(-10, -5.17) * mm});
            skArc(sketch, "E61.filletArc", {"start": v(-10, -4.72) * mm, "mid": v(-9.87, -5.04) * mm, "end": v(-9.55, -5.17) * mm});
            skLineSegment(sketch, "E62.bottom", {"start": v(-10.88, -4.42) * mm, "end": v(-12.08, -4.42) * mm});
            skLineSegment(sketch, "E62.top", {"start": v(-11.33, -5.17) * mm, "end": v(-11.63, -5.17) * mm});
            skLineSegment(sketch, "E62.left", {"start": v(-10.88, -4.42) * mm, "end": v(-10.88, -4.72) * mm});
            skLineSegment(sketch, "E62.right", {"start": v(-12.08, -4.42) * mm, "end": v(-12.08, -4.72) * mm});
            skPoint(sketch, "E63.visualSharp", {"position": v(-10.88, -5.17) * mm});
            skArc(sketch, "E63.filletArc", {"start": v(-11.33, -5.17) * mm, "mid": v(-11.01, -5.04) * mm, "end": v(-10.88, -4.72) * mm});
            skPoint(sketch, "E64.visualSharp", {"position": v(-12.08, -5.17) * mm});
            skArc(sketch, "E64.filletArc", {"start": v(-12.08, -4.72) * mm, "mid": v(-11.95, -5.04) * mm, "end": v(-11.63, -5.17) * mm});
            skLineSegment(sketch, "E65.bottom", {"start": v(-12.08, -4.42) * mm, "end": v(-12, -4.42) * mm});
            skLineSegment(sketch, "E65.top", {"start": v(-12.08, -1.42) * mm, "end": v(-12, -1.42) * mm});
            skLineSegment(sketch, "E65.left", {"start": v(-12.08, -4.42) * mm, "end": v(-12.08, -1.42) * mm});
            skLineSegment(sketch, "E65.right", {"start": v(-12, -4.42) * mm, "end": v(-12, -1.42) * mm});
            skLineSegment(sketch, "E66.bottom", {"start": v(1.68, -9) * mm, "end": v(-1.68, -9) * mm});
            skLineSegment(sketch, "E66.top", {"start": v(1.68, -6) * mm, "end": v(-1.68, -6) * mm});
            skLineSegment(sketch, "E66.left", {"start": v(1.68, -9) * mm, "end": v(1.68, -6) * mm});
            skLineSegment(sketch, "E66.right", {"start": v(-1.68, -9) * mm, "end": v(-1.68, -6) * mm});
            skSolve(sketch);
        }
        {
            var Q0;
            Q0=makeQuery(id+"F32.imprint","IMPRINT",FACE,{"disambiguationData":[TD([[makeQuery(id+"F32.imprint","IMPRINT",EDGE,{"derivedFrom":sQuery(id+"F32.wireOp",EDGE,"E27.bottom")}),1.0]])]});
            var Q1;
            Q1=makeQuery(id+"F32.imprint","IMPRINT",FACE,{"disambiguationData":[TD([[makeQuery(id+"F32.imprint","IMPRINT",EDGE,{"derivedFrom":sQuery(id+"F32.wireOp",EDGE,"E26.bottom")}),1.0]])]});
            var Q2;
            Q2=makeQuery(id+"F32.imprint","IMPRINT",FACE,{"disambiguationData":[TD([[makeQuery(id+"F32.imprint","IMPRINT",EDGE,{"derivedFrom":sQuery(id+"F32.wireOp",EDGE,"E29.top")}),-1.0]])]});
            var Q3;
            Q3=makeQuery(id+"F32.imprint","IMPRINT",FACE,{"disambiguationData":[TD([[makeQuery(id+"F32.imprint","IMPRINT",EDGE,{"derivedFrom":sQuery(id+"F32.wireOp",EDGE,"E28")}),-1.0]])]});
            var Q4;
            {var subQ1=sQuery(id+"F32.wireOp",EDGE,"E30.left");Q4=makeQuery(id+"F32.imprint","IMPRINT",FACE,{"disambiguationData":[TD([[makeQuery(id+"F32.imprint","IMPRINT",EDGE,{"derivedFrom":subQ1}),-1.0]])]});}
            var Q5;
            {var subQ1=sQuery(id+"F32.wireOp",EDGE,"E31.2.0.0");Q5=makeQuery(id+"F32.imprint","IMPRINT",FACE,{"disambiguationData":[TD([[makeQuery(id+"F32.imprint","IMPRINT",EDGE,{"derivedFrom":subQ1}),-1.0]])]});}
            var Q6;
            {var subQ1=sQuery(id+"F32.wireOp",EDGE,"E31.3.0.0");Q6=makeQuery(id+"F32.imprint","IMPRINT",FACE,{"disambiguationData":[TD([[makeQuery(id+"F32.imprint","IMPRINT",EDGE,{"derivedFrom":subQ1}),-1.0]])]});}
            var Q7;
            {var subQ1=sQuery(id+"F32.wireOp",EDGE,"E31.4.0.0");Q7=makeQuery(id+"F32.imprint","IMPRINT",FACE,{"disambiguationData":[TD([[makeQuery(id+"F32.imprint","IMPRINT",EDGE,{"derivedFrom":subQ1}),-1.0]])]});}
            var Q8;
            {var subQ0=sQuery(id+"F32.wireOp",EDGE,"E31.5.0.0");Q8=makeQuery(id+"F32.imprint","IMPRINT",FACE,{"disambiguationData":[TD([[makeQuery(id+"F32.imprint","IMPRINT",EDGE,{"derivedFrom":subQ0}),-1.0]])]});}
            var Q9;
            {var subQ1=sQuery(id+"F32.wireOp",EDGE,"E31.6.0.0");Q9=makeQuery(id+"F32.imprint","IMPRINT",FACE,{"disambiguationData":[TD([[makeQuery(id+"F32.imprint","IMPRINT",EDGE,{"derivedFrom":subQ1}),-1.0]])]});}
            var Q10;
            {var subQ0=sQuery(id+"F32.wireOp",EDGE,"E31.7.0.0");Q10=makeQuery(id+"F32.imprint","IMPRINT",FACE,{"disambiguationData":[TD([[makeQuery(id+"F32.imprint","IMPRINT",EDGE,{"derivedFrom":subQ0}),-1.0]])]});}
            var Q11;
            Q11=makeQuery(id+"F32.imprint","IMPRINT",FACE,{"disambiguationData":[TD([[makeQuery(id+"F32.imprint","IMPRINT",EDGE,{"derivedFrom":sQuery(id+"F32.wireOp",EDGE,"E65.bottom")}),1.0]])]});
            var Q12;
            {var subQ1=sQuery(id+"F32.wireOp",EDGE,"E31.8.0.0");Q12=makeQuery(id+"F32.imprint","IMPRINT",FACE,{"disambiguationData":[TD([[makeQuery(id+"F32.imprint","IMPRINT",EDGE,{"derivedFrom":subQ1}),-1.0]])]});}
            var Q13;
            {var subQ0=sQuery(id+"F32.wireOp",EDGE,"E31.9.0.0");Q13=makeQuery(id+"F32.imprint","IMPRINT",FACE,{"disambiguationData":[TD([[makeQuery(id+"F32.imprint","IMPRINT",EDGE,{"derivedFrom":subQ0}),-1.0]])]});}
            var Q14;
            Q14=makeQuery(id+"F32.imprint","IMPRINT",FACE,{"disambiguationData":[TD([[makeQuery(id+"F32.imprint","IMPRINT",EDGE,{"derivedFrom":sQuery(id+"F32.wireOp",EDGE,"E65.top")}),-1.0]])]});
            var Q15;
            Q15=makeQuery(id+"F32.imprint","IMPRINT",FACE,{"disambiguationData":[TD([[makeQuery(id+"F32.imprint","IMPRINT",EDGE,{"derivedFrom":sQuery(id+"F32.wireOp",EDGE,"E62.top")}),-1.0]])]});
            extrude(context, id + "F33", {"entities" : qUnion([Q0, Q1, Q2, Q3, Q4, Q5, Q6, Q7, Q8, Q9, Q10, Q11, Q12, Q13, Q14, Q15]), "operationType" : NewBodyOperationType.ADD, "oppositeDirection" : true, "depth" : 6 * mm});
        }
        {
            var Q0;
            Q0=makeQuery(id+"F33.opExtrude","CAP_EDGE",EDGE,{"disambiguationData":[OSD([sQuery(id+"F32.wireOp",EDGE,"E26.bottom")])],"isStart":false});
            var Q1;
            Q1=makeQuery(id+"F33.opExtrude","CAP_EDGE",EDGE,{"disambiguationData":[OSD([sQuery(id+"F32.wireOp",EDGE,"E27.bottom"),sQuery(id+"F32.wireOp",EDGE,"E65.top")])],"isStart":false});
            fillet(context, id + "F34", {"entities" : qUnion([Q0, Q1]), "radius" : 1.5 * mm, "tangentPropagation" : true, "allowEdgeOverflow" : false});
        }
        {
            var Q0;
            {var subQ0=sQuery(id+"F20.wireOp",EDGE,"E20.right");var subQ1=sQuery(id+"F20.wireOp",EDGE,"E20.top");var subQ2=sQuery(id+"F20.wireOp",EDGE,"E20.bottom");var subQ3=sQuery(id+"F17.wireOp",EDGE,"E16");var subQ4=sQuery(id+"F0.wireOp",EDGE,"E0.right");var subQ5=sQuery(id+"F0.wireOp",EDGE,"E0.left");var subQ6=sQuery(id+"F0.wireOp",EDGE,"E0.top");var subQ7=sQuery(id+"F0.wireOp",EDGE,"E0.bottom");var subQ8=makeQuery(id+"F21.opExtrude","CAP_FACE",FACE,{"disambiguationData":[OSD([subQ7,subQ6,subQ5,subQ4,subQ3,sQuery(id+"F17.wireOp",EDGE,"E17"),subQ2,subQ1,sQuery(id+"F20.wireOp",EDGE,"E20.left"),subQ0])],"isStart":false});Q0=makeQuery(id+"F29.boolean.opBoolean","SPLIT",FACE,{"disambiguationData":[TD([makeQuery(id+"F21.opExtrude","SWEPT_FACE",FACE,{"disambiguationData":[OSD([subQ0])]})])],"derivedFrom":subQ8});}
            var sketch = newSketch(context, id + "F35", { "sketchPlane" : qUnion([Q0])});
            skLineSegment(sketch, "E67", {"start": v(16, 16.5) * mm, "end": v(35.15, 0.43) * mm});
            skLineSegment(sketch, "E68", {"start": v(16, 4.5) * mm, "end": v(35.15, -11.57) * mm});
            skLineSegment(sketch, "E69", {"start": v(35.15, 0.43) * mm, "end": v(35.15, -11.57) * mm});
            skLineSegment(sketch, "E70", {"start": v(16, 16.5) * mm, "end": v(16, 4.5) * mm});
            skSolve(sketch);
        }
        {
            var Q0;
            {var subQ8=sQuery(id+"F35.wireOp",EDGE,"E67");Q0=makeQuery(id+"F35.imprint","IMPRINT",FACE,{"disambiguationData":[TD([[makeQuery(id+"F35.imprint","IMPRINT",EDGE,{"derivedFrom":subQ8}),-1.0]])]});}
            extrude(context, id + "F36", {"entities" : qUnion([Q0]), "operationType" : NewBodyOperationType.ADD, "depth" : 13 * mm});
        }
        {
            var Q0;
            Q0=makeQuery(id+"F36.opExtrude","SWEPT_EDGE",EDGE,{"disambiguationData":[OSD([sQuery(id+"F35.wireOp",EDGE,"E67"),sQuery(id+"F35.wireOp",EDGE,"E69")])]});
            fillet(context, id + "F37", {"entities" : qUnion([Q0]), "radius" : 5 * mm, "tangentPropagation" : true, "allowEdgeOverflow" : false});
        }
        {
            var Q0;
            Q0=makeQuery(id+"F36.opExtrude","SWEPT_EDGE",EDGE,{"disambiguationData":[OSD([sQuery(id+"F35.wireOp",EDGE,"E68"),sQuery(id+"F35.wireOp",EDGE,"E69")])]});
            fillet(context, id + "F38", {"entities" : qUnion([Q0]), "radius" : 4 * mm, "tangentPropagation" : true, "allowEdgeOverflow" : false});
        }
        {
            var Q0;
            Q0=makeQuery(id+"F36.boolean.opBoolean","MERGE",FACE,{"derivedFrom":[makeQuery(id+"F22.opExtrude","CAP_FACE",FACE,{"disambiguationData":[OSD([sQuery(id+"F0.wireOp",EDGE,"E0.bottom"),sQuery(id+"F0.wireOp",EDGE,"E0.top"),sQuery(id+"F0.wireOp",EDGE,"E0.left"),sQuery(id+"F0.wireOp",EDGE,"E0.right"),sQuery(id+"F17.wireOp",EDGE,"E16"),sQuery(id+"F17.wireOp",EDGE,"E17"),sQuery(id+"F20.wireOp",EDGE,"E20.bottom"),sQuery(id+"F20.wireOp",EDGE,"E20.top"),sQuery(id+"F20.wireOp",EDGE,"E20.left"),sQuery(id+"F20.wireOp",EDGE,"E20.right")])],"isStart":false}),makeQuery(id+"F36.opExtrude","CAP_FACE",FACE,{"disambiguationData":[OSD([sQuery(id+"F35.wireOp",EDGE,"E67"),sQuery(id+"F35.wireOp",EDGE,"E68"),sQuery(id+"F35.wireOp",EDGE,"E69"),sQuery(id+"F35.wireOp",EDGE,"E70")])],"isStart":false})]});
            var sketch = newSketch(context, id + "F39", { "sketchPlane" : qUnion([Q0])});
            skCircle(sketch, "E71", {"center": v(31, -2.15) * mm, "radius": 1.65 * mm});
            skSolve(sketch);
        }
        {
            var Q0;
            Q0=makeQuery(id+"F39.imprint","IMPRINT",FACE,{"disambiguationData":[TD([[makeQuery(id+"F39.imprint","IMPRINT",EDGE,{"derivedFrom":sQuery(id+"F39.wireOp",EDGE,"E71")}),1.0]])]});
            extrude(context, id + "F40", {"entities" : qUnion([Q0]), "operationType" : NewBodyOperationType.REMOVE, "endBound" : BoundingType.UP_TO_NEXT, "oppositeDirection" : true, "depth" : 25 * mm});
        }
    });
